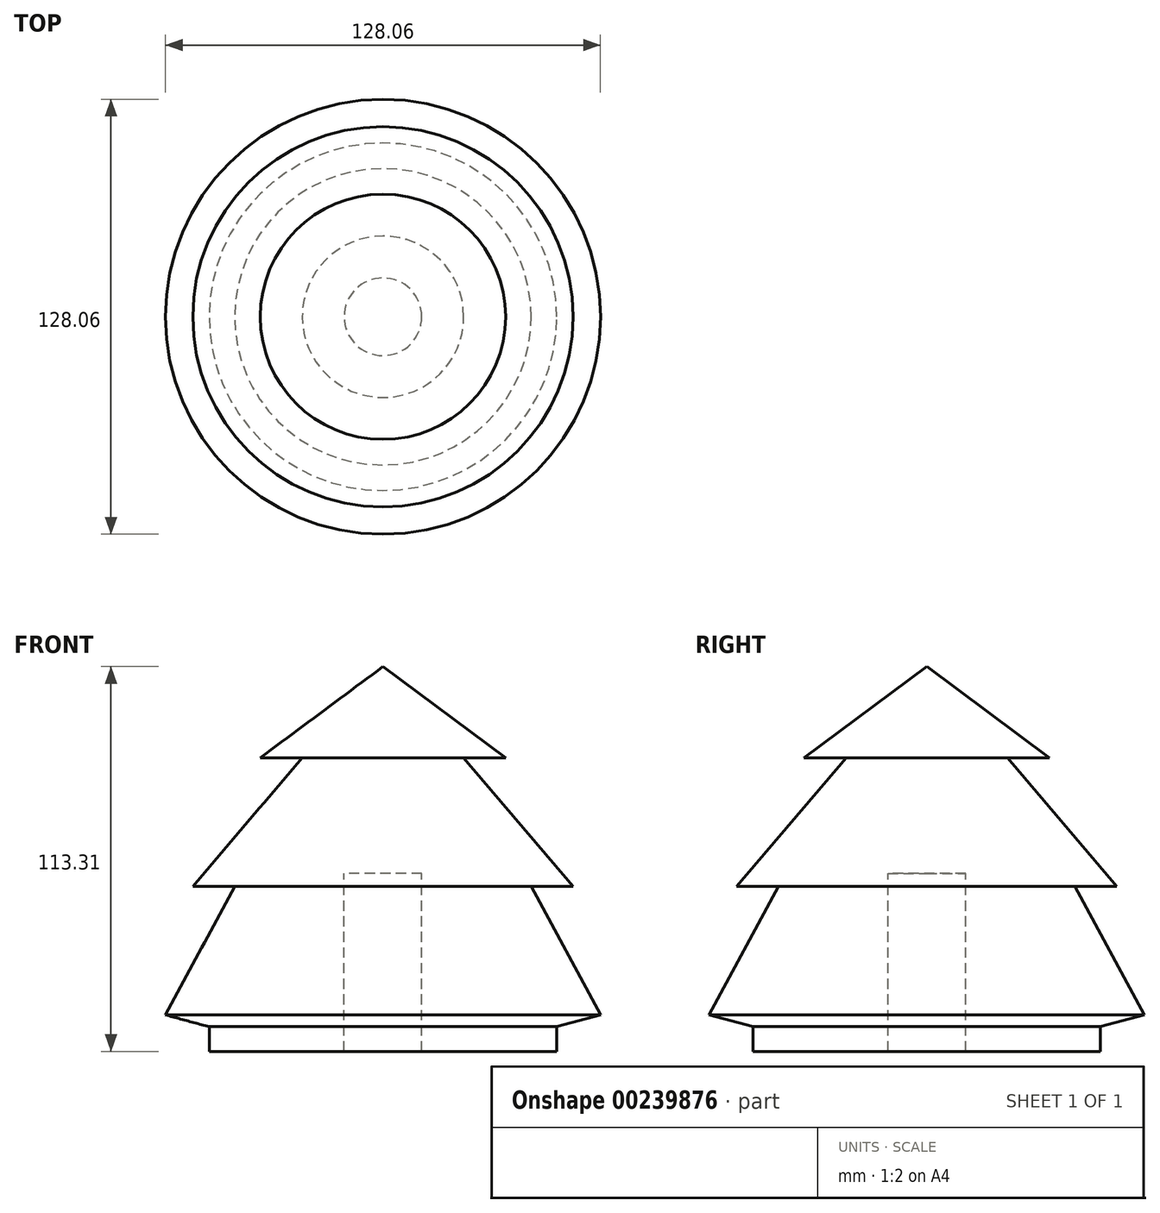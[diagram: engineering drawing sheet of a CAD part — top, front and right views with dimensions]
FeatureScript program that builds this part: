
annotation { "Feature Type Name" : "Feature", "Feature Type Description" : "" }
export const myFeature = defineFeature(function(context is Context, id is Id, definition is map)
    precondition{}
    {
        {
            var Q0;
            Q0=qCreatedBy(makeId("Front.planeOp"),FACE);
            var sketch = newSketch(context, id + "F0", { "sketchPlane" : qUnion([Q0])});
            skLineSegment(sketch, "E0", {"start": v(0, 60.95) * mm, "end": v(-36.11, 34.1) * mm});
            skLineSegment(sketch, "E1", {"start": v(-36.11, 34.1) * mm, "end": v(-23.76, 34.1) * mm});
            skLineSegment(sketch, "E2", {"start": v(-23.76, 34.1) * mm, "end": v(-55.98, -3.76) * mm});
            skLineSegment(sketch, "E3", {"start": v(-55.98, -3.76) * mm, "end": v(-43.63, -3.76) * mm});
            skLineSegment(sketch, "E4", {"start": v(-43.63, -3.76) * mm, "end": v(-64.03, -41.62) * mm});
            skLineSegment(sketch, "E5", {"start": v(-64.03, -41.62) * mm, "end": v(-51.15, -45.1) * mm});
            skLineSegment(sketch, "E6", {"start": v(-51.15, -45.1) * mm, "end": v(-51.15, -52.36) * mm});
            skLineSegment(sketch, "E7", {"start": v(-51.15, -52.36) * mm, "end": v(0, -52.36) * mm});
            skLineSegment(sketch, "E8", {"start": v(0, -52.36) * mm, "end": v(0, 60.95) * mm});
            skSolve(sketch);
        }
        {
            var Q0;
            Q0=makeQuery(id+"F0.imprint","IMPRINT",FACE,{"disambiguationData":[TD([[makeQuery(id+"F0.imprint","IMPRINT",EDGE,{"derivedFrom":sQuery(id+"F0.wireOp",EDGE,"E0")}),1.0]])]});
            var Q1;
            Q1=sQuery(id+"F0.wireOp",EDGE,"E8");
            revolve(context, id + "F1", {"entities" : qUnion([Q0]), "axis" : qUnion([Q1]), "revolveType" : RevolveType.FULL});
        }
        {
            var Q0;
            Q0=qCreatedBy(makeId("Top.planeOp"),FACE);
            var sketch = newSketch(context, id + "F2", { "sketchPlane" : qUnion([Q0])});
            skCircle(sketch, "E9", {"center": v(0, 0) * mm, "radius": 11.43 * mm});
            skSolve(sketch);
        }
        {
            var Q0;
            Q0 = qSketchRegion(id + "F2", true);
            extrude(context, id + "F3", {"entities" : qUnion([Q0]), "operationType" : NewBodyOperationType.REMOVE, "oppositeDirection" : true, "depth" : 122.94 * mm});
        }
    });
